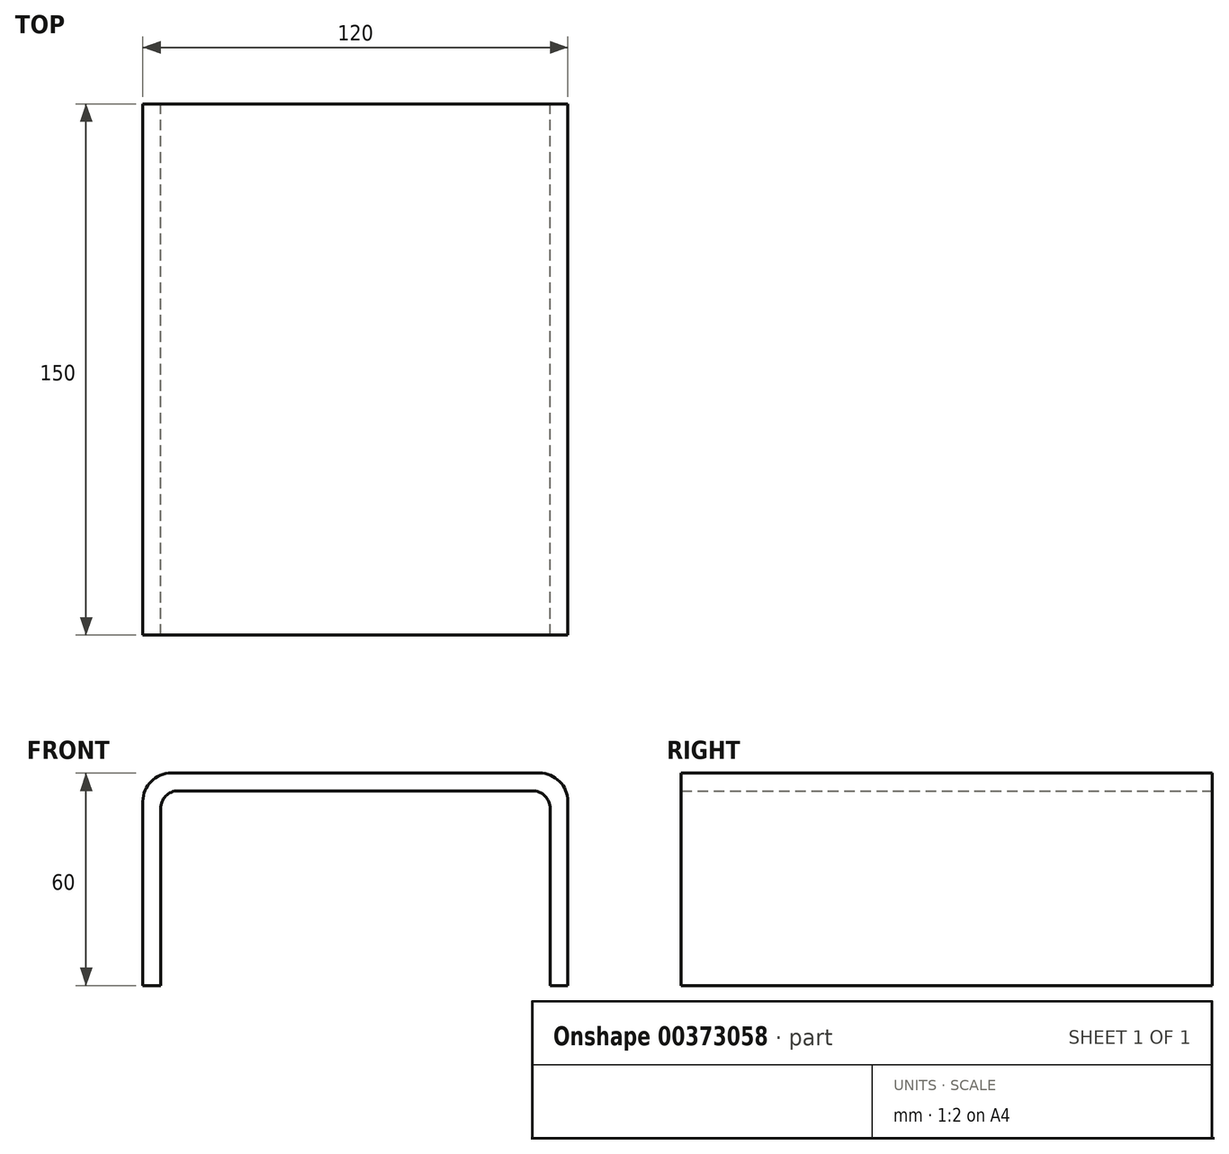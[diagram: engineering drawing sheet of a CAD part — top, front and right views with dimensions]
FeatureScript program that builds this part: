
annotation { "Feature Type Name" : "Feature", "Feature Type Description" : "" }
export const myFeature = defineFeature(function(context is Context, id is Id, definition is map)
    precondition{}
    {
        {
            var Q0;
            Q0=qCreatedBy(makeId("Front.planeOp"),FACE);
            var sketch = newSketch(context, id + "F0", { "sketchPlane" : qUnion([Q0])});
            skLineSegment(sketch, "E0", {"start": v(-66.23, 0) * mm, "end": v(-66.23, 52) * mm});
            skLineSegment(sketch, "E1", {"start": v(-58.23, 60) * mm, "end": v(45.77, 60) * mm});
            skLineSegment(sketch, "E2", {"start": v(53.77, 52) * mm, "end": v(53.77, 0) * mm});
            skLineSegment(sketch, "E3.0", {"start": v(48.77, 50) * mm, "end": v(48.77, 0) * mm});
            skLineSegment(sketch, "E3.1", {"start": v(-56.23, 55) * mm, "end": v(43.77, 55) * mm});
            skLineSegment(sketch, "E3.2", {"start": v(-61.23, 0) * mm, "end": v(-61.23, 50) * mm});
            skLineSegment(sketch, "E4", {"start": v(-66.23, 0) * mm, "end": v(-61.23, 0) * mm});
            skLineSegment(sketch, "E5", {"start": v(48.77, 0) * mm, "end": v(53.77, 0) * mm});
            skPoint(sketch, "E6.visualSharp", {"position": v(-61.23, 55) * mm});
            skArc(sketch, "E6.filletArc", {"start": v(-56.23, 55) * mm, "mid": v(-59.77, 53.54) * mm, "end": v(-61.23, 50) * mm});
            skPoint(sketch, "E7.visualSharp", {"position": v(48.77, 55) * mm});
            skArc(sketch, "E7.filletArc", {"start": v(48.77, 50) * mm, "mid": v(47.3, 53.54) * mm, "end": v(43.77, 55) * mm});
            skPoint(sketch, "E8.visualSharp", {"position": v(-66.23, 60) * mm});
            skArc(sketch, "E8.filletArc", {"start": v(-58.23, 60) * mm, "mid": v(-63.89, 57.66) * mm, "end": v(-66.23, 52) * mm});
            skPoint(sketch, "E9.visualSharp", {"position": v(53.77, 60) * mm});
            skArc(sketch, "E9.filletArc", {"start": v(53.77, 52) * mm, "mid": v(51.42, 57.66) * mm, "end": v(45.77, 60) * mm});
            skSolve(sketch);
        }
        {
            var Q0;
            Q0 = qSketchRegion(id + "F0", true);
            extrude(context, id + "F1", {"entities" : qUnion([Q0]), "endBound" : BoundingType.SYMMETRIC, "depth" : 150 * mm});
        }
    });
